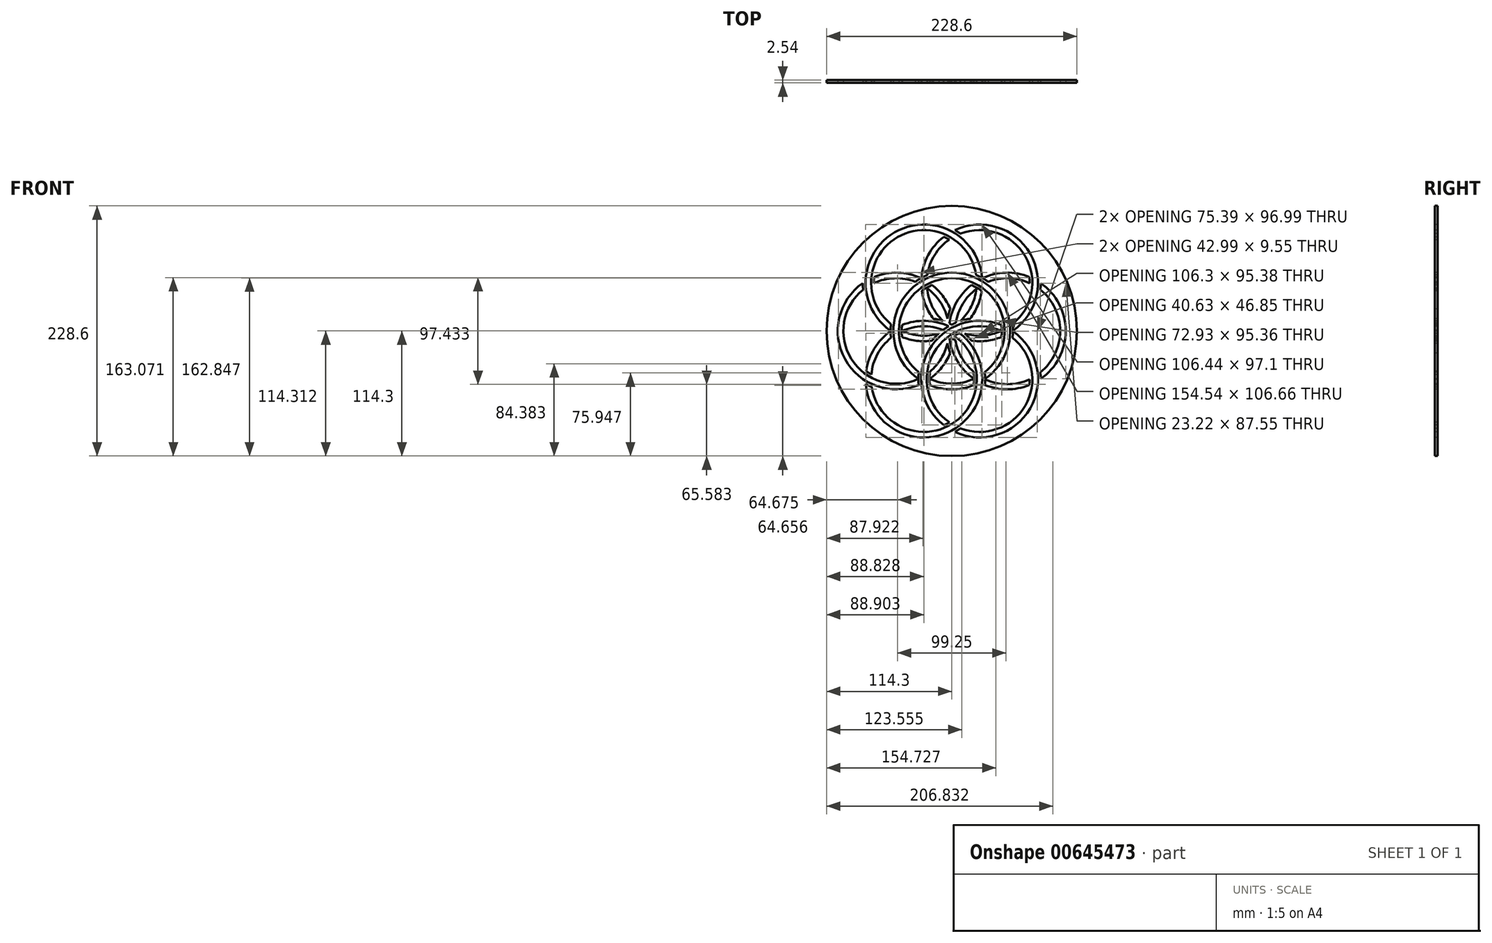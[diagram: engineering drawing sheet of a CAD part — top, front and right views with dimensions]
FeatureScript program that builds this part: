
annotation { "Feature Type Name" : "Feature", "Feature Type Description" : "" }
export const myFeature = defineFeature(function(context is Context, id is Id, definition is map)
    precondition{}
    {
        {
            var Q0;
            Q0=qCreatedBy(makeId("Front.planeOp"),FACE);
            var sketch = newSketch(context, id + "F0", { "sketchPlane" : qUnion([Q0])});
            skPoint(sketch, "E0.middle", {"position": v(0, 0) * mm});
            skCircle(sketch, "E1", {"center": v(0, 0) * mm, "radius": 114.3 * mm});
            skSolve(sketch);
        }
        {
            var Q0;
            Q0 = qSketchRegion(id + "F0", true);
            extrude(context, id + "F1", {"entities" : qUnion([Q0]), "depth" : -2.54 * mm, "offsetDistance" : 25.4 * mm});
        }
        {
            var Q0;
            Q0=qCreatedBy(makeId("Front.planeOp"),FACE);
            var sketch = newSketch(context, id + "F2", { "sketchPlane" : qUnion([Q0])});
            skCircle(sketch, "E2", {"center": v(0, 0) * mm, "radius": 101.6 * mm, "construction": true});
            skLineSegment(sketch, "E3", {"start": v(-101.6, 0) * mm, "end": v(101.6, 0) * mm, "construction": true});
            skLineSegment(sketch, "E4", {"start": v(50.8, 87.99) * mm, "end": v(-50.8, -87.99) * mm, "construction": true});
            skLineSegment(sketch, "E5", {"start": v(-50.8, 87.99) * mm, "end": v(50.8, -87.99) * mm, "construction": true});
            skCircle(sketch, "E6", {"center": v(0, 0) * mm, "radius": 50.8 * mm, "construction": true});
            skCircle(sketch, "E7", {"center": v(-25.4, 44) * mm, "radius": 50.8 * mm, "construction": true});
            skCircle(sketch, "E8", {"center": v(25.4, 44) * mm, "radius": 50.8 * mm, "construction": true});
            skCircle(sketch, "E9", {"center": v(50.8, 0) * mm, "radius": 50.8 * mm, "construction": true});
            skCircle(sketch, "E10", {"center": v(25.4, -44) * mm, "radius": 50.8 * mm, "construction": true});
            skCircle(sketch, "E11", {"center": v(-25.4, -44) * mm, "radius": 50.8 * mm, "construction": true});
            skCircle(sketch, "E12", {"center": v(-50.8, 0) * mm, "radius": 50.8 * mm, "construction": true});
            skArc(sketch, "E13", {"start": v(-30.12, -37.7) * mm, "mid": v(0, 48.26) * mm, "end": v(30.12, -37.7) * mm});
            skArc(sketch, "E14", {"start": v(-55.52, 6.3) * mm, "mid": v(-49.53, 85.79) * mm, "end": v(22.31, 51.23) * mm});
            skArc(sketch, "E15", {"start": v(2.35, -4.51) * mm, "mid": v(0, -85.03) * mm, "end": v(-73.11, -51.23) * mm});
            skPoint(sketch, "E15.startSnap0", {"position": v(0, 48.26) * mm});
            skArc(sketch, "E16", {"start": v(-80.92, 37.7) * mm, "mid": v(-91.83, -25.4) * mm, "end": v(-30.48, -43.77) * mm});
            skArc(sketch, "E17", {"start": v(-81.28, 43.77) * mm, "mid": v(-97.56, -25.67) * mm, "end": v(-30.24, -49.22) * mm});
            skArc(sketch, "E18", {"start": v(-30.48, -43.77) * mm, "mid": v(0, 53.34) * mm, "end": v(30.48, -43.77) * mm});
            skArc(sketch, "E19", {"start": v(7.43, -1.95) * mm, "mid": v(0, -90.9) * mm, "end": v(-78.55, -48.5) * mm});
            skArc(sketch, "E20", {"start": v(-55.88, 0.22) * mm, "mid": v(-52.07, 90.19) * mm, "end": v(27.75, 48.5) * mm});
            skArc(sketch, "E21", {"start": v(7.81, 88.93) * mm, "mid": v(67.2, 68.12) * mm, "end": v(55.52, 6.3) * mm});
            skArc(sketch, "E22", {"start": v(2.73, 92.28) * mm, "mid": v(71.6, 70.66) * mm, "end": v(55.88, 0.22) * mm});
            skArc(sketch, "E23", {"start": v(-2.35, 83.48) * mm, "mid": v(-15.63, 69.4) * mm, "end": v(-22.31, 51.23) * mm});
            skArc(sketch, "E24", {"start": v(-7.43, 86.03) * mm, "mid": v(-21.5, 69.39) * mm, "end": v(-27.75, 48.5) * mm});
            skArc(sketch, "E25", {"start": v(-71.12, 43.77) * mm, "mid": v(-52.28, 48.24) * mm, "end": v(-33.21, 44.94) * mm});
            skArc(sketch, "E26", {"start": v(-70.8, 49.45) * mm, "mid": v(-49.34, 53.32) * mm, "end": v(-28.13, 48.28) * mm});
            skArc(sketch, "E27", {"start": v(81.28, -43.77) * mm, "mid": v(104.14, 0) * mm, "end": v(81.28, 43.77) * mm});
            skArc(sketch, "E28", {"start": v(80.92, 37.7) * mm, "mid": v(99.06, 0) * mm, "end": v(80.92, -37.7) * mm});
            skArc(sketch, "E29", {"start": v(45.4, 5.46) * mm, "mid": v(-20.8, -17.32) * mm, "end": v(-7.43, -86.03) * mm});
            skArc(sketch, "E30", {"start": v(-2.35, -83.48) * mm, "mid": v(-16.4, -19.86) * mm, "end": v(45.72, -0.22) * mm});
            skArc(sketch, "E31", {"start": v(55.52, -6.3) * mm, "mid": v(67.2, -68.12) * mm, "end": v(7.81, -88.93) * mm});
            skArc(sketch, "E32", {"start": v(55.88, -0.22) * mm, "mid": v(71.6, -70.66) * mm, "end": v(2.73, -92.28) * mm});
            skCircle(sketch, "E33", {"center": v(0, 0) * mm, "radius": 55.88 * mm, "construction": true});
            skCircle(sketch, "E34", {"center": v(-50.8, 0) * mm, "radius": 55.88 * mm, "construction": true});
            skCircle(sketch, "E35", {"center": v(25.4, -44) * mm, "radius": 55.88 * mm, "construction": true});
            skCircle(sketch, "E36", {"center": v(-25.4, 44) * mm, "radius": 55.88 * mm, "construction": true});
            skCircle(sketch, "E37", {"center": v(50.8, 0) * mm, "radius": 55.88 * mm, "construction": true});
            skCircle(sketch, "E38", {"center": v(-25.4, -44) * mm, "radius": 55.88 * mm, "construction": true});
            skCircle(sketch, "E39", {"center": v(25.4, 44) * mm, "radius": 55.88 * mm, "construction": true});
            skArc(sketch, "E40", {"start": v(81.28, 43.77) * mm, "mid": v(81.18, 40.73) * mm, "end": v(80.92, 37.7) * mm});
            skArc(sketch, "E41", {"start": v(-81.28, 43.77) * mm, "mid": v(-81.18, 40.73) * mm, "end": v(-80.92, 37.7) * mm});
            skArc(sketch, "E42", {"start": v(-33.21, 44.94) * mm, "mid": v(-30.72, 46.68) * mm, "end": v(-28.13, 48.28) * mm});
            skArc(sketch, "E43", {"start": v(-22.31, 51.23) * mm, "mid": v(-25.07, 49.94) * mm, "end": v(-27.75, 48.5) * mm});
            skArc(sketch, "E44", {"start": v(55.52, 6.3) * mm, "mid": v(55.78, 3.26) * mm, "end": v(55.88, 0.22) * mm});
            skArc(sketch, "E45", {"start": v(55.52, -6.3) * mm, "mid": v(55.78, -3.26) * mm, "end": v(55.88, -0.22) * mm});
            skArc(sketch, "E46", {"start": v(22.31, 51.23) * mm, "mid": v(25.07, 49.94) * mm, "end": v(27.75, 48.5) * mm});
            skArc(sketch, "E47", {"start": v(-55.52, 6.3) * mm, "mid": v(-55.78, 3.26) * mm, "end": v(-55.88, 0.22) * mm});
            skArc(sketch, "E48", {"start": v(-30.12, -37.7) * mm, "mid": v(-30.38, -40.73) * mm, "end": v(-30.48, -43.77) * mm});
            skArc(sketch, "E49", {"start": v(30.12, -37.7) * mm, "mid": v(30.38, -40.73) * mm, "end": v(30.48, -43.77) * mm});
            skArc(sketch, "E50", {"start": v(-30.24, -49.22) * mm, "mid": v(-30.42, -46.5) * mm, "end": v(-30.48, -43.77) * mm});
            skCircle(sketch, "E51", {"center": v(-25.4, 44) * mm, "radius": 45.72 * mm, "construction": true});
            skCircle(sketch, "E52", {"center": v(0, 0) * mm, "radius": 45.72 * mm, "construction": true});
            skCircle(sketch, "E53", {"center": v(25.4, 44) * mm, "radius": 45.72 * mm, "construction": true});
            skCircle(sketch, "E54", {"center": v(50.8, 0) * mm, "radius": 45.72 * mm, "construction": true});
            skCircle(sketch, "E55", {"center": v(25.4, -44) * mm, "radius": 45.72 * mm, "construction": true});
            skCircle(sketch, "E56", {"center": v(-25.4, -44) * mm, "radius": 45.72 * mm, "construction": true});
            skCircle(sketch, "E57", {"center": v(-50.8, 0) * mm, "radius": 45.72 * mm, "construction": true});
            skArc(sketch, "E58", {"start": v(-70.8, 49.45) * mm, "mid": v(-71.04, 46.62) * mm, "end": v(-71.12, 43.77) * mm});
            skArc(sketch, "E59", {"start": v(-7.43, 86.03) * mm, "mid": v(-4.85, 84.84) * mm, "end": v(-2.35, 83.48) * mm});
            skArc(sketch, "E60", {"start": v(2.73, 92.28) * mm, "mid": v(5.32, 90.67) * mm, "end": v(7.81, 88.93) * mm});
            skArc(sketch, "E61", {"start": v(-73.11, -51.23) * mm, "mid": v(-75.87, -49.94) * mm, "end": v(-78.55, -48.5) * mm});
            skArc(sketch, "E62", {"start": v(-7.43, -86.03) * mm, "mid": v(-4.85, -84.84) * mm, "end": v(-2.35, -83.48) * mm});
            skArc(sketch, "E63", {"start": v(7.81, -88.93) * mm, "mid": v(5.32, -90.67) * mm, "end": v(2.73, -92.28) * mm});
            skArc(sketch, "E64", {"start": v(80.92, -37.7) * mm, "mid": v(81.18, -40.73) * mm, "end": v(81.28, -43.77) * mm});
            skArc(sketch, "E65", {"start": v(45.4, 5.46) * mm, "mid": v(45.64, 2.62) * mm, "end": v(45.72, -0.22) * mm});
            skArc(sketch, "E66", {"start": v(-55.52, -6.3) * mm, "mid": v(-67.92, -21.16) * mm, "end": v(-73.47, -39.7) * mm});
            skArc(sketch, "E67", {"start": v(-78.22, -36.58) * mm, "mid": v(-70.85, -16.07) * mm, "end": v(-55.88, -0.22) * mm});
            skArc(sketch, "E68", {"start": v(-45.4, 5.46) * mm, "mid": v(-23.94, 9.33) * mm, "end": v(-2.73, 4.29) * mm});
            skArc(sketch, "E69", {"start": v(-45.72, -0.22) * mm, "mid": v(-26.88, 4.24) * mm, "end": v(-7.81, 0.95) * mm});
            skArc(sketch, "E70", {"start": v(-73.47, -39.7) * mm, "mid": v(-75.9, -38.22) * mm, "end": v(-78.22, -36.58) * mm});
            skArc(sketch, "E71", {"start": v(-55.52, -6.3) * mm, "mid": v(-55.78, -3.26) * mm, "end": v(-55.88, -0.22) * mm});
            skArc(sketch, "E72", {"start": v(-45.72, -0.22) * mm, "mid": v(-45.64, 2.62) * mm, "end": v(-45.4, 5.46) * mm});
            skArc(sketch, "E73", {"start": v(-7.81, 0.95) * mm, "mid": v(-5.32, 2.69) * mm, "end": v(-2.73, 4.29) * mm});
            skArc(sketch, "E74", {"start": v(7.43, -1.95) * mm, "mid": v(4.85, -3.15) * mm, "end": v(2.35, -4.51) * mm});
            skArc(sketch, "E75", {"start": v(33.21, 44.94) * mm, "mid": v(52.28, 48.24) * mm, "end": v(71.12, 43.77) * mm});
            skArc(sketch, "E76", {"start": v(70.8, 49.45) * mm, "mid": v(49.34, 53.32) * mm, "end": v(28.13, 48.28) * mm});
            skArc(sketch, "E77", {"start": v(17.97, 42.04) * mm, "mid": v(4.45, 26.4) * mm, "end": v(-2.1, 6.8) * mm});
            skArc(sketch, "E78", {"start": v(23.54, 39.2) * mm, "mid": v(10.36, 25.37) * mm, "end": v(3.65, 7.48) * mm});
            skPoint(sketch, "E78.startSnap0", {"position": v(14.62, 39.2) * mm});
            skArc(sketch, "E79", {"start": v(-20.32, -43.7) * mm, "mid": v(0, -48.19) * mm, "end": v(20.32, -43.7) * mm});
            skArc(sketch, "E80", {"start": v(-20, -49.45) * mm, "mid": v(0, -53.34) * mm, "end": v(20, -49.45) * mm});
            skArc(sketch, "E81", {"start": v(20.32, -43.77) * mm, "mid": v(5.35, -27.92) * mm, "end": v(-2.02, -7.41) * mm});
            skArc(sketch, "E82", {"start": v(71.12, -44.18) * mm, "mid": v(50.8, -48.63) * mm, "end": v(30.48, -44.18) * mm});
            skArc(sketch, "E83", {"start": v(70.8, -49.45) * mm, "mid": v(50.5, -53.34) * mm, "end": v(30.24, -49.22) * mm});
            skArc(sketch, "E84", {"start": v(-19.78, -36.97) * mm, "mid": v(-9.8, -25.45) * mm, "end": v(-3.9, -11.4) * mm});
            skArc(sketch, "E85", {"start": v(-20.32, -43.77) * mm, "mid": v(-9.12, -33.28) * mm, "end": v(-1.37, -20.03) * mm});
            skArc(sketch, "E86", {"start": v(-22.68, 39.7) * mm, "mid": v(-18.1, 23.06) * mm, "end": v(-7.95, 9.1) * mm});
            skArc(sketch, "E87", {"start": v(-27.42, 36.58) * mm, "mid": v(-23.71, 23.18) * mm, "end": v(-16.67, 11.2) * mm});
            skArc(sketch, "E88", {"start": v(45.72, 0.22) * mm, "mid": v(29, -4.13) * mm, "end": v(11.82, -2.32) * mm});
            skArc(sketch, "E89", {"start": v(45.4, -5.46) * mm, "mid": v(31.93, -8.94) * mm, "end": v(18.03, -8.83) * mm});
            skArc(sketch, "E90", {"start": v(27.42, 36.58) * mm, "mid": v(23.71, 23.18) * mm, "end": v(16.67, 11.2) * mm});
            skArc(sketch, "E91", {"start": v(22.67, 39.7) * mm, "mid": v(18.08, 23.05) * mm, "end": v(7.92, 9.08) * mm});
            skArc(sketch, "E92", {"start": v(-45.72, 0.22) * mm, "mid": v(-29, -4.13) * mm, "end": v(-11.82, -2.32) * mm});
            skArc(sketch, "E93", {"start": v(-45.4, -5.46) * mm, "mid": v(-31.93, -8.94) * mm, "end": v(-18.03, -8.83) * mm});
            skArc(sketch, "E94", {"start": v(71.12, -44.18) * mm, "mid": v(71.03, -46.82) * mm, "end": v(70.8, -49.45) * mm});
            skArc(sketch, "E95", {"start": v(30.24, -49.22) * mm, "mid": v(30.41, -46.7) * mm, "end": v(30.48, -44.18) * mm});
            skArc(sketch, "E96", {"start": v(28.13, 48.28) * mm, "mid": v(30.72, 46.68) * mm, "end": v(33.21, 44.94) * mm});
            skArc(sketch, "E97", {"start": v(70.8, 49.45) * mm, "mid": v(71.04, 46.62) * mm, "end": v(71.12, 43.77) * mm});
            skArc(sketch, "E98", {"start": v(-27.42, 36.58) * mm, "mid": v(-25.1, 38.21) * mm, "end": v(-22.68, 39.7) * mm});
            skArc(sketch, "E99", {"start": v(-16.67, 11.2) * mm, "mid": v(-12.26, 10.32) * mm, "end": v(-7.95, 9.1) * mm});
            skArc(sketch, "E100", {"start": v(-20.32, -43.7) * mm, "mid": v(-20.25, -46.58) * mm, "end": v(-20, -49.45) * mm});
            skArc(sketch, "E101", {"start": v(20.32, -43.7) * mm, "mid": v(20.25, -46.58) * mm, "end": v(20, -49.45) * mm});
            skArc(sketch, "E102", {"start": v(-3.9, -11.4) * mm, "mid": v(-2.8, -15.77) * mm, "end": v(-1.37, -20.03) * mm});
            skArc(sketch, "E103", {"start": v(-19.78, -36.97) * mm, "mid": v(-20.18, -40.36) * mm, "end": v(-20.32, -43.77) * mm});
            skArc(sketch, "E104", {"start": v(19.78, -36.97) * mm, "mid": v(9, -24.13) * mm, "end": v(3.27, -8.38) * mm});
            skArc(sketch, "E105", {"start": v(-23.05, 39.48) * mm, "mid": v(-10.92, 27.18) * mm, "end": v(-3.9, 11.4) * mm});
            skArc(sketch, "E106", {"start": v(-1.37, 20.03) * mm, "mid": v(-8.22, 32.13) * mm, "end": v(-17.97, 42.04) * mm});
            skArc(sketch, "E107", {"start": v(-3.9, 11.4) * mm, "mid": v(-2.8, 15.77) * mm, "end": v(-1.37, 20.03) * mm});
            skArc(sketch, "E108", {"start": v(-17.97, 42.04) * mm, "mid": v(-20.55, 40.84) * mm, "end": v(-23.05, 39.48) * mm});
            skArc(sketch, "E109", {"start": v(17.97, 42.04) * mm, "mid": v(20.8, 40.71) * mm, "end": v(23.54, 39.2) * mm});
            skArc(sketch, "E110", {"start": v(27.42, 36.58) * mm, "mid": v(25.1, 38.22) * mm, "end": v(22.67, 39.7) * mm});
            skArc(sketch, "E111", {"start": v(-45.4, -5.46) * mm, "mid": v(-45.64, -2.62) * mm, "end": v(-45.72, 0.22) * mm});
            skArc(sketch, "E112", {"start": v(-11.82, -2.32) * mm, "mid": v(-15.06, -5.45) * mm, "end": v(-18.03, -8.83) * mm});
            skArc(sketch, "E113", {"start": v(19.78, -36.97) * mm, "mid": v(20.18, -40.36) * mm, "end": v(20.32, -43.77) * mm});
            skArc(sketch, "E114", {"start": v(45.4, -5.46) * mm, "mid": v(45.63, -2.84) * mm, "end": v(45.72, -0.22) * mm});
            skArc(sketch, "E115", {"start": v(11.82, -2.32) * mm, "mid": v(15.06, -5.45) * mm, "end": v(18.03, -8.83) * mm});
            skArc(sketch, "E116", {"start": v(7.92, 9.08) * mm, "mid": v(12.25, 10.32) * mm, "end": v(16.67, 11.2) * mm});
            skArc(sketch, "E117", {"start": v(3.27, -8.38) * mm, "mid": v(1.24, -7.48) * mm, "end": v(-0.75, -6.5) * mm});
            skArc(sketch, "E118", {"start": v(-0.75, -6.5) * mm, "mid": v(-1.4, -6.95) * mm, "end": v(-2.02, -7.41) * mm});
            skArc(sketch, "E119", {"start": v(-2.1, 6.8) * mm, "mid": v(-1.05, 6.3) * mm, "end": v(0, 5.78) * mm});
            skArc(sketch, "E120", {"start": v(3.65, 7.48) * mm, "mid": v(1.8, 6.66) * mm, "end": v(0, 5.78) * mm});
            skSolve(sketch);
        }
        {
            var Q0;
            Q0 = qSketchRegion(id + "F2", true);
            extrude(context, id + "F3", {"entities" : qUnion([Q0]), "operationType" : NewBodyOperationType.REMOVE, "endBound" : BoundingType.THROUGH_ALL, "oppositeDirection" : true, "depth" : 25.4 * mm, "offsetDistance" : 25.4 * mm});
        }
    });
